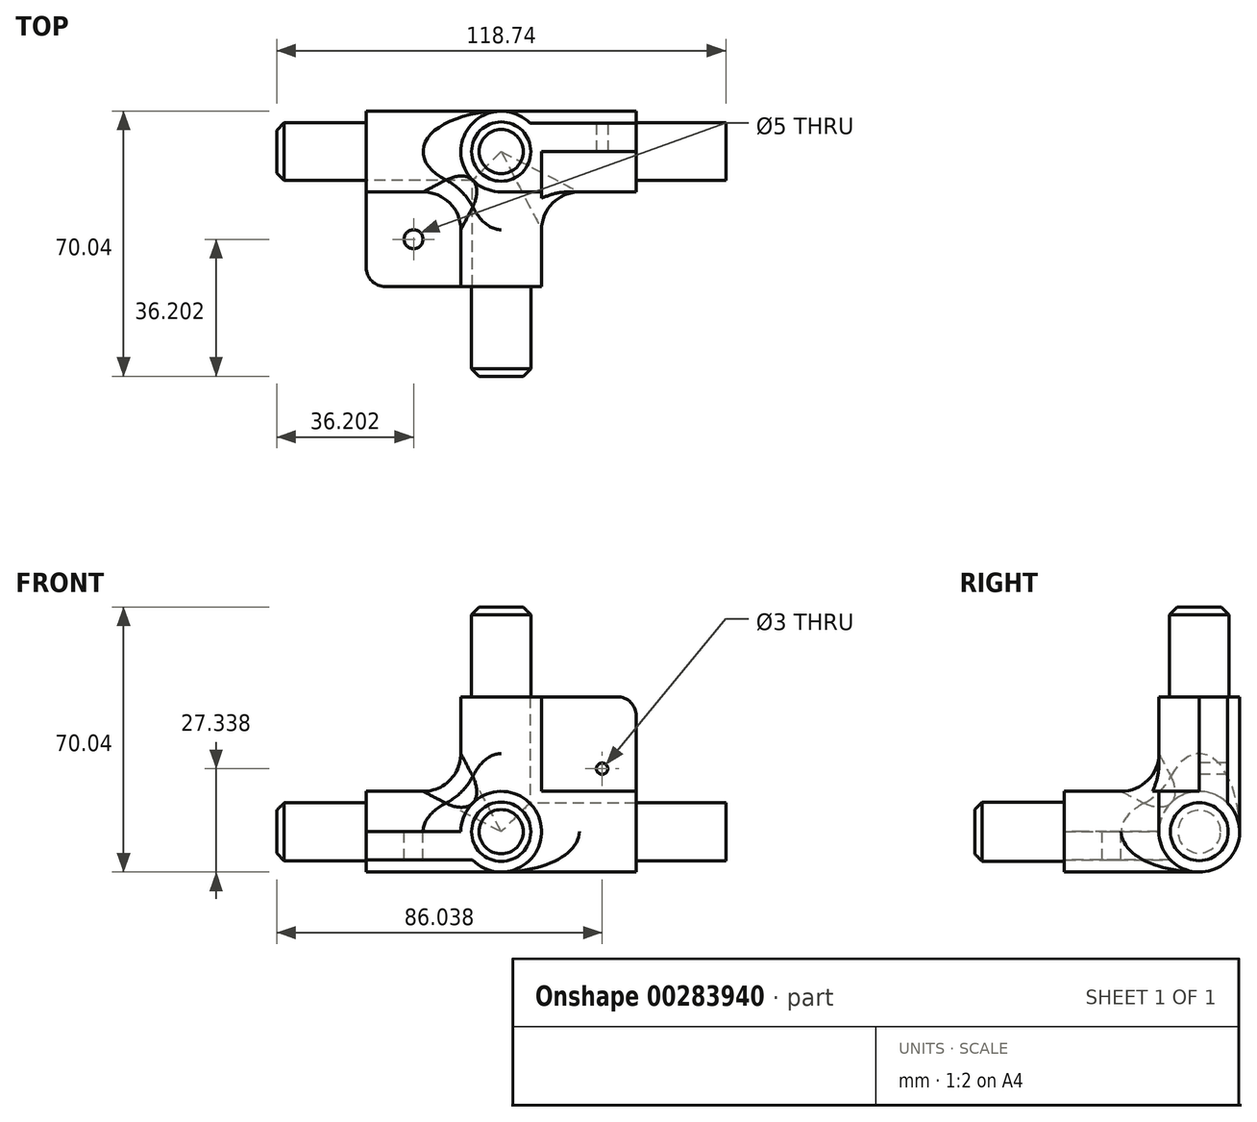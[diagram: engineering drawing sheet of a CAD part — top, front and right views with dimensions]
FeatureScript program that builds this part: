
annotation { "Feature Type Name" : "Feature", "Feature Type Description" : "" }
export const myFeature = defineFeature(function(context is Context, id is Id, definition is map)
    precondition{}
    {
        {
            var Q0;
            Q0=qCreatedBy(makeId("Right.planeOp"),FACE);
            var sketch = newSketch(context, id + "F0", { "sketchPlane" : qUnion([Q0])});
            skCircle(sketch, "E0", {"center": v(0, 0) * mm, "radius": 10.67 * mm});
            skSolve(sketch);
        }
        {
            var Q0;
            Q0=qSketchRegion(id+"F0",true);
            extrude(context, id + "F1", {"entities" : qUnion([Q0]), "endBound" : BoundingType.SYMMETRIC, "depth" : 21.34 * mm + 20 * mm});
        }
        {
            var Q0;
            Q0=makeQuery(id+"F1.opExtrude","CAP_FACE",FACE,{"disambiguationData":[OSD([sQuery(id+"F0.wireOp",EDGE,"E0")])],"isStart":false});
            var sketch = newSketch(context, id + "F2", { "sketchPlane" : qUnion([Q0])});
            skCircle(sketch, "E1", {"center": v(0, 0) * mm, "radius": 7.9 * mm});
            skSolve(sketch);
        }
        {
            var Q0;
            Q0=qSketchRegion(id+"F2",true);
            extrude(context, id + "F3", {"entities" : qUnion([Q0]), "operationType" : NewBodyOperationType.ADD, "depth" : 15.8 * mm * 1.5 + 15 * mm});
        }
        {
            var Q0;
            Q0=makeQuery(id+"F3.opExtrude","CAP_FACE",FACE,{"disambiguationData":[OSD([sQuery(id+"F2.wireOp",EDGE,"E1")])],"isStart":false});
            var sketch = newSketch(context, id + "F4", { "sketchPlane" : qUnion([Q0])});
            skCircle(sketch, "E2.0", {"center": v(0, 0) * mm, "radius": 7.9 * mm});
            skCircle(sketch, "E3", {"center": v(0, 0) * mm, "radius": 7.65 * mm});
            skSolve(sketch);
        }
        {
            var Q0;
            Q0=qSketchRegion(id+"F4",true);
            var Q1;
            Q1=makeQuery(id+"F1.opExtrude","CAP_FACE",FACE,{"disambiguationData":[OSD([sQuery(id+"F0.wireOp",EDGE,"E0")])],"isStart":false});
            extrude(context, id + "F5", {"entities" : qUnion([Q0]), "operationType" : NewBodyOperationType.REMOVE, "endBound" : BoundingType.UP_TO_SURFACE, "oppositeDirection" : true, "endBoundEntityFace" : qUnion([Q1]), "depth" : 25 * mm});
        }
        {
            var Q0;
            Q0=makeQuery(id+"F1.opExtrude","CAP_FACE",FACE,{"disambiguationData":[OSD([sQuery(id+"F0.wireOp",EDGE,"E0")])],"isStart":true});
            var sketch = newSketch(context, id + "F6", { "sketchPlane" : qUnion([Q0])});
            skCircle(sketch, "E4", {"center": v(0, 0) * mm, "radius": 7.65 * mm});
            skSolve(sketch);
        }
        {
            var Q0;
            Q0=qSketchRegion(id+"F6",true);
            extrude(context, id + "F7", {"entities" : qUnion([Q0]), "operationType" : NewBodyOperationType.ADD, "depth" : 15.8 * mm * 1.5 + 15 * mm});
        }
        {
            var Q0;
            Q0=qCreatedBy(makeId("Top.planeOp"),FACE);
            var sketch = newSketch(context, id + "F8", { "sketchPlane" : qUnion([Q0])});
            skCircle(sketch, "E5", {"center": v(0, 0) * mm, "radius": 10.67 * mm});
            skSolve(sketch);
        }
        {
            var Q0;
            Q0=qSketchRegion(id+"F8",true);
            extrude(context, id + "F9", {"entities" : qUnion([Q0]), "operationType" : NewBodyOperationType.ADD, "depth" : 21.34 * mm / 2 + 25 * mm});
        }
        {
            var Q0;
            Q0=makeQuery(id+"F9.opExtrude","CAP_FACE",FACE,{"disambiguationData":[OSD([sQuery(id+"F8.wireOp",EDGE,"E5")])],"isStart":false});
            var sketch = newSketch(context, id + "F10", { "sketchPlane" : qUnion([Q0])});
            skCircle(sketch, "E6", {"center": v(0, 0) * mm, "radius": 7.84 * mm});
            skSolve(sketch);
        }
        {
            var Q0;
            Q0=qSketchRegion(id+"F10",true);
            extrude(context, id + "F11", {"entities" : qUnion([Q0]), "operationType" : NewBodyOperationType.ADD, "depth" : 15.8 * mm * 1.5});
        }
        {
            var Q0;
            Q0=qCreatedBy(makeId("Front.planeOp"),FACE);
            var sketch = newSketch(context, id + "F12", { "sketchPlane" : qUnion([Q0])});
            skCircle(sketch, "E7", {"center": v(0, 0) * mm, "radius": 10.67 * mm});
            skSolve(sketch);
        }
        {
            var Q0;
            Q0=qSketchRegion(id+"F12",true);
            extrude(context, id + "F13", {"entities" : qUnion([Q0]), "operationType" : NewBodyOperationType.ADD, "depth" : 21.34 * mm / 2 + 10 * mm});
        }
        {
            var Q0;
            Q0=makeQuery(id+"F13.opExtrude","CAP_FACE",FACE,{"disambiguationData":[OSD([sQuery(id+"F12.wireOp",EDGE,"E7")])],"isStart":false});
            var sketch = newSketch(context, id + "F14", { "sketchPlane" : qUnion([Q0])});
            skCircle(sketch, "E8", {"center": v(0, 0) * mm, "radius": 7.84 * mm});
            skSolve(sketch);
        }
        {
            var Q0;
            Q0=qSketchRegion(id+"F14",true);
            extrude(context, id + "F15", {"entities" : qUnion([Q0]), "operationType" : NewBodyOperationType.ADD, "depth" : 15.8 * mm * 1.5 + 15 * mm});
        }
        {
            var Q0;
            Q0=makeQuery(id+"F11.opExtrude","CAP_EDGE",EDGE,{"disambiguationData":[OSD([sQuery(id+"F10.wireOp",EDGE,"E6")])],"isStart":false});
            var Q1;
            Q1=makeQuery(id+"F5.boolean.opBoolean","COPY",EDGE,{"derivedFrom":makeQuery(id+"F5.opExtrude","CAP_EDGE",EDGE,{"disambiguationData":[OSD([sQuery(id+"F4.wireOp",EDGE,"E3")])],"isStart":true})});
            var Q2;
            Q2=makeQuery(id+"F7.opExtrude","CAP_EDGE",EDGE,{"disambiguationData":[OSD([sQuery(id+"F6.wireOp",EDGE,"E4")])],"isStart":false});
            var Q3;
            Q3=makeQuery(id+"F15.opExtrude","CAP_EDGE",EDGE,{"disambiguationData":[OSD([sQuery(id+"F14.wireOp",EDGE,"E8")])],"isStart":false});
            chamfer(context, id + "F16", {"entities" : qUnion([Q0, Q1, Q2, Q3]), "width" : 2 * mm, "tangentPropagation" : true});
        }
        {
            var Q0;
            Q0=makeQuery(id+"F13.opExtrude","CAP_FACE",FACE,{"disambiguationData":[OSD([sQuery(id+"F12.wireOp",EDGE,"E7")])],"isStart":false});
            extrude(context, id + "F17", {"entities" : qUnion([Q0]), "operationType" : NewBodyOperationType.ADD, "depth" : 15 * mm});
        }
        {
            var Q0;
            Q0=makeQuery(id+"F1.opExtrude","CAP_FACE",FACE,{"disambiguationData":[OSD([sQuery(id+"F0.wireOp",EDGE,"E0")])],"isStart":true});
            extrude(context, id + "F18", {"entities" : qUnion([Q0]), "operationType" : NewBodyOperationType.ADD, "depth" : 15 * mm});
        }
        {
            var Q0;
            Q0=qCreatedBy(makeId("Top.planeOp"),FACE);
            var sketch = newSketch(context, id + "F19", { "sketchPlane" : qUnion([Q0])});
            skLineSegment(sketch, "E9.bottom", {"start": v(0, 0) * mm, "end": v(-35.67, 0) * mm});
            skLineSegment(sketch, "E9.top", {"start": v(0, -35.67) * mm, "end": v(-35.67, -35.67) * mm});
            skLineSegment(sketch, "E9.left", {"start": v(0, 0) * mm, "end": v(0, -35.67) * mm});
            skLineSegment(sketch, "E9.right", {"start": v(-35.67, 0) * mm, "end": v(-35.67, -35.67) * mm});
            skLineSegment(sketch, "E10.0", {"start": v(10.67, -35.67) * mm, "end": v(-10.67, -35.67) * mm, "construction": true});
            skLineSegment(sketch, "E10.1", {"start": v(-35.67, 10.67) * mm, "end": v(-35.67, -10.67) * mm, "construction": true});
            skSolve(sketch);
        }
        {
            var Q0;
            Q0 = qSketchRegion(id + "F19", true);
            extrude(context, id + "F20", {"entities" : qUnion([Q0]), "operationType" : NewBodyOperationType.ADD, "oppositeDirection" : true, "depth" : 7.5 * mm});
        }
        {
            var Q0;
            Q0=makeQuery(id+"F20.opExtrude","CAP_FACE",FACE,{"disambiguationData":[OSD([sQuery(id+"F19.wireOp",EDGE,"E9.bottom"),sQuery(id+"F19.wireOp",EDGE,"E9.top"),sQuery(id+"F19.wireOp",EDGE,"E9.left"),sQuery(id+"F19.wireOp",EDGE,"E9.right")])],"isStart":true});
            var sketch = newSketch(context, id + "F21", { "sketchPlane" : qUnion([Q0])});
            skLineSegment(sketch, "E11", {"start": v(-23.17, -10.67) * mm, "end": v(-23.17, -35.67) * mm, "construction": true});
            skPoint(sketch, "E11.endSnap0", {"position": v(-23.17, -35.67) * mm});
            skCircle(sketch, "E12", {"center": v(-23.17, -23.17) * mm, "radius": 2.5 * mm});
            skSolve(sketch);
        }
        {
            var Q0;
            Q0 = qSketchRegion(id + "F21", true);
            extrude(context, id + "F22", {"entities" : qUnion([Q0]), "operationType" : NewBodyOperationType.REMOVE, "endBound" : BoundingType.THROUGH_ALL, "oppositeDirection" : true, "depth" : 25 * mm});
        }
        {
            var Q0;
            {var subQ0=sQuery(id+"F0.wireOp",EDGE,"E0");Q0=makeQuery(id+"F5.boolean.opBoolean","MERGE",FACE,{"derivedFrom":[makeQuery(id+"F1.opExtrude","CAP_FACE",FACE,{"disambiguationData":[OSD([subQ0])],"isStart":false}),makeQuery(id+"F5.opExtrude","CAP_FACE",FACE,{"disambiguationData":[OSD([subQ0])],"isStart":false})]});}
            extrude(context, id + "F23", {"entities" : qUnion([Q0]), "operationType" : NewBodyOperationType.ADD, "depth" : 15 * mm});
        }
        {
            var Q0;
            Q0=qCreatedBy(makeId("Front.planeOp"),FACE);
            var sketch = newSketch(context, id + "F24", { "sketchPlane" : qUnion([Q0])});
            skLineSegment(sketch, "E13.0", {"start": v(-10.67, 35.67) * mm, "end": v(10.67, 35.67) * mm, "construction": true});
            skLineSegment(sketch, "E13.1", {"start": v(35.67, 10.67) * mm, "end": v(35.67, -10.67) * mm, "construction": true});
            skLineSegment(sketch, "E14.bottom", {"start": v(0, 0) * mm, "end": v(35.67, 0) * mm});
            skLineSegment(sketch, "E14.top", {"start": v(0, 35.67) * mm, "end": v(35.67, 35.67) * mm});
            skLineSegment(sketch, "E14.left", {"start": v(0, 0) * mm, "end": v(0, 35.67) * mm});
            skLineSegment(sketch, "E14.right", {"start": v(35.67, 0) * mm, "end": v(35.67, 35.67) * mm});
            skSolve(sketch);
        }
        {
            var Q0;
            Q0 = qSketchRegion(id + "F24", true);
            extrude(context, id + "F25", {"entities" : qUnion([Q0]), "operationType" : NewBodyOperationType.ADD, "oppositeDirection" : true, "depth" : 7.5 * mm});
        }
        {
            var Q0;
            Q0=makeQuery(id+"F25.boolean.opBoolean","MERGE",FACE,{"derivedFrom":[makeQuery(id+"F23.opExtrude","CAP_FACE",FACE,{"disambiguationData":[OSD([sQuery(id+"F0.wireOp",EDGE,"E0")])],"isStart":false}),makeQuery(id+"F25.opExtrude","SWEPT_FACE",FACE,{"disambiguationData":[OSD([sQuery(id+"F24.wireOp",EDGE,"E14.right")])]})]});
            var sketch = newSketch(context, id + "F26", { "sketchPlane" : qUnion([Q0])});
            skArc(sketch, "E15.0", {"start": v(0, 10.67) * mm, "mid": v(-7.54, 7.54) * mm, "end": v(-10.67, 0) * mm});
            skLineSegment(sketch, "E16", {"start": v(0, 10.67) * mm, "end": v(-10.67, 10.67) * mm});
            skLineSegment(sketch, "E17", {"start": v(-10.67, 10.67) * mm, "end": v(-10.67, 0) * mm});
            skLineSegment(sketch, "E18", {"start": v(-10.67, 0) * mm, "end": v(0, 0) * mm, "construction": true});
            skPoint(sketch, "E19.orphan", {"position": v(7.5, 7.59) * mm});
            skSolve(sketch);
        }
        {
            var Q0;
            Q0 = qSketchRegion(id + "F26", true);
            extrude(context, id + "F27", {"entities" : qUnion([Q0]), "operationType" : NewBodyOperationType.ADD, "endBound" : BoundingType.UP_TO_NEXT, "oppositeDirection" : true, "depth" : 30 * mm});
        }
        {
            var Q0;
            Q0=makeQuery(id+"F25.boolean.opBoolean","MERGE",FACE,{"derivedFrom":[makeQuery(id+"F9.opExtrude","CAP_FACE",FACE,{"disambiguationData":[OSD([sQuery(id+"F8.wireOp",EDGE,"E5")])],"isStart":false}),makeQuery(id+"F25.opExtrude","SWEPT_FACE",FACE,{"disambiguationData":[OSD([sQuery(id+"F24.wireOp",EDGE,"E14.top")])]})]});
            var sketch = newSketch(context, id + "F28", { "sketchPlane" : qUnion([Q0])});
            skArc(sketch, "E20.0", {"start": v(0, -10.67) * mm, "mid": v(7.54, -7.54) * mm, "end": v(10.67, 0) * mm});
            skLineSegment(sketch, "E21", {"start": v(10.67, -10.67) * mm, "end": v(0, -10.67) * mm});
            skLineSegment(sketch, "E22", {"start": v(0, -10.67) * mm, "end": v(0, 0) * mm, "construction": true});
            skPoint(sketch, "E23.orphan", {"position": v(7.59, 7.5) * mm});
            skPoint(sketch, "E24.orphan", {"position": v(35.67, 0) * mm});
            skLineSegment(sketch, "E25", {"start": v(10.67, 0) * mm, "end": v(10.67, -10.67) * mm});
            skSolve(sketch);
        }
        {
            var Q0;
            Q0 = qSketchRegion(id + "F28", true);
            var Q1;
            Q1=makeQuery(id+"F27.opExtrude","SWEPT_FACE",FACE,{"disambiguationData":[OSD([sQuery(id+"F26.wireOp",EDGE,"E16")])]});
            extrude(context, id + "F29", {"entities" : qUnion([Q0]), "operationType" : NewBodyOperationType.ADD, "endBound" : BoundingType.UP_TO_SURFACE, "oppositeDirection" : true, "endBoundEntityFace" : qUnion([Q1]), "depth" : 25 * mm});
        }
        {
            var Q0;
            Q0=makeQuery(id+"F20.opExtrude","SWEPT_EDGE",EDGE,{"disambiguationData":[OSD([sQuery(id+"F19.wireOp",EDGE,"E9.top"),sQuery(id+"F19.wireOp",EDGE,"E9.right")])]});
            var Q1;
            Q1=makeQuery(id+"F25.opExtrude","SWEPT_EDGE",EDGE,{"disambiguationData":[OSD([sQuery(id+"F24.wireOp",EDGE,"E14.top"),sQuery(id+"F24.wireOp",EDGE,"E14.right")])]});
            fillet(context, id + "F30", {"entities" : qUnion([Q0, Q1]), "radius" : 5 * mm, "tangentPropagation" : true, "allowEdgeOverflow" : false});
        }
        {
            var Q0;
            Q0=makeQuery(id+"F9.boolean.opBoolean","INTERSECT",EDGE,{"disambiguationData":[OD(0.0)],"derivedFrom":[makeQuery(id+"F1.opExtrude","SWEPT_FACE",FACE,{"disambiguationData":[OSD([sQuery(id+"F0.wireOp",EDGE,"E0")])]}),makeQuery(id+"F9.opExtrude","SWEPT_FACE",FACE,{"disambiguationData":[OSD([sQuery(id+"F8.wireOp",EDGE,"E5")])]})]});
            var Q1;
            {var subQ0=sQuery(id+"F12.wireOp",EDGE,"E7");var subQ1=makeQuery(id+"F13.opExtrude","SWEPT_FACE",FACE,{"disambiguationData":[OSD([subQ0])]});var subQ2=sQuery(id+"F0.wireOp",EDGE,"E0");var subQ3=makeQuery(id+"F1.opExtrude","SWEPT_FACE",FACE,{"disambiguationData":[OSD([subQ2])]});Q1=makeQuery(id+"F20.boolean.opBoolean","SPLIT",EDGE,{"disambiguationData":[TD([makeQuery(id+"F9.opExtrude","SWEPT_FACE",FACE,{"disambiguationData":[OSD([sQuery(id+"F8.wireOp",EDGE,"E5")])]})])],"derivedFrom":makeQuery(id+"F13.boolean.opBoolean","INTERSECT",EDGE,{"disambiguationData":[OD(0.0)],"derivedFrom":[subQ3,subQ1]})});}
            var Q2;
            Q2=makeQuery(id+"F13.boolean.opBoolean","INTERSECT",EDGE,{"disambiguationData":[OD(1.0)],"derivedFrom":[makeQuery(id+"F1.opExtrude","SWEPT_FACE",FACE,{"disambiguationData":[OSD([sQuery(id+"F0.wireOp",EDGE,"E0")])]}),makeQuery(id+"F13.opExtrude","SWEPT_FACE",FACE,{"disambiguationData":[OSD([sQuery(id+"F12.wireOp",EDGE,"E7")])]})]});
            fillet(context, id + "F31", {"entities" : qUnion([Q0, Q1, Q2]), "radius" : 10 * mm, "tangentPropagation" : true, "allowEdgeOverflow" : false});
        }
        {
            var Q0;
            Q0=makeQuery(id+"F25.opExtrude","CAP_FACE",FACE,{"disambiguationData":[OSD([sQuery(id+"F24.wireOp",EDGE,"E14.bottom"),sQuery(id+"F24.wireOp",EDGE,"E14.top"),sQuery(id+"F24.wireOp",EDGE,"E14.left"),sQuery(id+"F24.wireOp",EDGE,"E14.right")])],"isStart":true});
            var sketch = newSketch(context, id + "F32", { "sketchPlane" : qUnion([Q0])});
            skCircle(sketch, "E26", {"center": v(26.67, 16.67) * mm, "radius": 1.5 * mm});
            skSolve(sketch);
        }
        {
            var Q0;
            Q0 = qSketchRegion(id + "F32", true);
            extrude(context, id + "F33", {"entities" : qUnion([Q0]), "operationType" : NewBodyOperationType.REMOVE, "endBound" : BoundingType.THROUGH_ALL, "oppositeDirection" : true, "depth" : 25 * mm});
        }
    });
